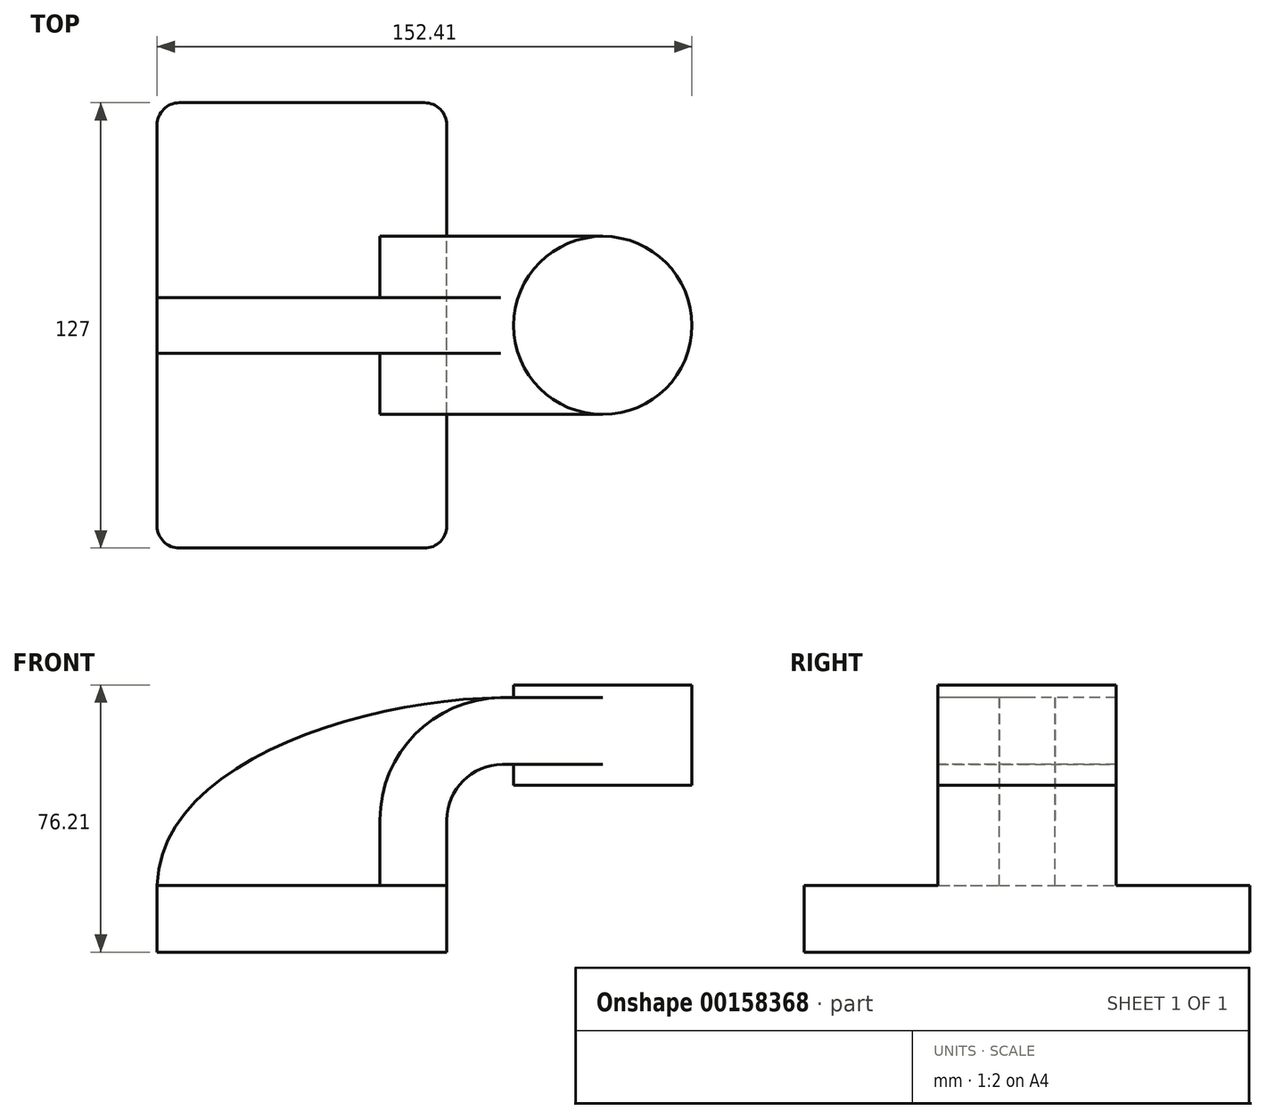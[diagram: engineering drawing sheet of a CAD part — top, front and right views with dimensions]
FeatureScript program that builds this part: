
annotation { "Feature Type Name" : "Feature", "Feature Type Description" : "" }
export const myFeature = defineFeature(function(context is Context, id is Id, definition is map)
    precondition{}
    {
        {
            var Q0;
            Q0=qCreatedBy(makeId("Front.planeOp"),FACE);
            var sketch = newSketch(context, id + "F0", { "sketchPlane" : qUnion([Q0])});
            skLineSegment(sketch, "E0.bottom", {"start": v(41.28, -9.52) * mm, "end": v(-41.28, -9.53) * mm});
            skLineSegment(sketch, "E0.top", {"start": v(41.28, 9.53) * mm, "end": v(-41.28, 9.53) * mm});
            skLineSegment(sketch, "E0.left", {"start": v(41.28, -9.52) * mm, "end": v(41.28, 9.53) * mm});
            skLineSegment(sketch, "E0.right", {"start": v(-41.28, -9.53) * mm, "end": v(-41.28, 9.53) * mm});
            skPoint(sketch, "E0.middle", {"position": v(0, 0) * mm});
            skLineSegment(sketch, "E1", {"start": v(41.28, 9.53) * mm, "end": v(41.28, 28.1) * mm});
            skArc(sketch, "E2", {"start": v(41.28, 28.1) * mm, "mid": v(45.92, 39.33) * mm, "end": v(57.15, 43.98) * mm});
            skLineSegment(sketch, "E3.bottom", {"start": v(111.12, 38.1) * mm, "end": v(60.32, 38.1) * mm});
            skLineSegment(sketch, "E3.top", {"start": v(111.12, 66.67) * mm, "end": v(60.32, 66.67) * mm});
            skLineSegment(sketch, "E3.left", {"start": v(111.12, 38.1) * mm, "end": v(111.12, 66.68) * mm});
            skLineSegment(sketch, "E3.right", {"start": v(60.32, 38.1) * mm, "end": v(60.32, 66.68) * mm});
            skPoint(sketch, "E3.middle", {"position": v(85.72, 52.39) * mm});
            skLineSegment(sketch, "E4", {"start": v(57.15, 43.98) * mm, "end": v(85.73, 43.98) * mm});
            skLineSegment(sketch, "E5.0", {"start": v(57.15, 63.03) * mm, "end": v(85.73, 63.03) * mm});
            skArc(sketch, "E5.1", {"start": v(22.23, 28.1) * mm, "mid": v(32.45, 52.8) * mm, "end": v(57.15, 63.03) * mm});
            skLineSegment(sketch, "E5.2", {"start": v(22.22, 9.53) * mm, "end": v(22.22, 28.1) * mm});
            skLineSegment(sketch, "E6", {"start": v(85.72, 38.1) * mm, "end": v(85.72, 66.67) * mm});
            skFitSpline(sketch, "E7", {"points": [v(-41.28, 9.53) * mm, v(57.15, 63.03) * mm], "startDerivative": vector(2.16, 105.35) * mm, "endDerivative": vector(117.88, 0.68) * mm});
            skSolve(sketch);
        }
        {
            var Q0;
            Q0=makeQuery(id+"F0.imprint","IMPRINT",FACE,{"disambiguationData":[TD([[makeQuery(id+"F0.imprint","IMPRINT",EDGE,{"derivedFrom":sQuery(id+"F0.wireOp",EDGE,"E0.bottom")}),-1.0]])]});
            extrude(context, id + "F1", {"entities" : qUnion([Q0]), "endBound" : BoundingType.SYMMETRIC, "depth" : 127 * mm});
        }
        {
            var Q0;
            {var subQ9=sQuery(id+"F0.wireOp",EDGE,"E1");Q0=makeQuery(id+"F0.imprint","IMPRINT",FACE,{"disambiguationData":[TD([[makeQuery(id+"F0.imprint","IMPRINT",EDGE,{"derivedFrom":subQ9}),1.0]])]});}
            var Q1;
            {var subQ0=sQuery(id+"F0.wireOp",EDGE,"E4");var subQ1=sQuery(id+"F0.wireOp",EDGE,"E3.right");var subQ2=makeQuery(id+"F0.imprint","INTERSECT",VERTEX,{"derivedFrom":[subQ1,subQ0]});Q1=makeQuery(id+"F0.imprint","IMPRINT",FACE,{"disambiguationData":[TD([[makeQuery(id+"F0.imprint","IMPRINT",EDGE,{"disambiguationData":[TD([[subQ2,-1.0]])],"derivedFrom":subQ1}),-1.0]])]});}
            extrude(context, id + "F2", {"entities" : qUnion([Q0, Q1]), "operationType" : NewBodyOperationType.ADD, "endBound" : BoundingType.SYMMETRIC, "depth" : 50.8 * mm});
        }
        {
            var Q0;
            {var subQ3=sQuery(id+"F0.wireOp",EDGE,"E5.2");Q0=makeQuery(id+"F0.imprint","IMPRINT",FACE,{"disambiguationData":[TD([[makeQuery(id+"F0.imprint","IMPRINT",EDGE,{"derivedFrom":subQ3}),1.0]])]});}
            extrude(context, id + "F3", {"entities" : qUnion([Q0]), "operationType" : NewBodyOperationType.ADD, "endBound" : BoundingType.SYMMETRIC, "depth" : 15.88 * mm});
        }
        {
            var Q0;
            {var subQ0=sQuery(id+"F0.wireOp",EDGE,"E3.left");Q0=makeQuery(id+"F0.imprint","IMPRINT",FACE,{"disambiguationData":[TD([[makeQuery(id+"F0.imprint","IMPRINT",EDGE,{"derivedFrom":subQ0}),1.0]])]});}
            var Q1;
            Q1=sQuery(id+"F0.wireOp",EDGE,"E6");
            revolve(context, id + "F4", {"operationType" : NewBodyOperationType.ADD, "entities" : qUnion([Q0]), "axis" : qUnion([Q1]), "revolveType" : RevolveType.FULL});
        }
        {
            var Q0;
            Q0=makeQuery(id+"F1.opExtrude","CAP_EDGE",EDGE,{"disambiguationData":[OSD([sQuery(id+"F0.wireOp",EDGE,"E0.right")])],"isStart":false});
            var Q1;
            Q1=makeQuery(id+"F1.opExtrude","CAP_EDGE",EDGE,{"disambiguationData":[OSD([sQuery(id+"F0.wireOp",EDGE,"E0.left")])],"isStart":false});
            var Q2;
            Q2=makeQuery(id+"F1.opExtrude","CAP_EDGE",EDGE,{"disambiguationData":[OSD([sQuery(id+"F0.wireOp",EDGE,"E0.left")])],"isStart":true});
            var Q3;
            Q3=makeQuery(id+"F1.opExtrude","CAP_EDGE",EDGE,{"disambiguationData":[OSD([sQuery(id+"F0.wireOp",EDGE,"E0.right")])],"isStart":true});
            fillet(context, id + "F5", {"entities" : qUnion([Q0, Q1, Q2, Q3]), "radius" : 6.35 * mm, "tangentPropagation" : true, "allowEdgeOverflow" : false});
        }
    });
